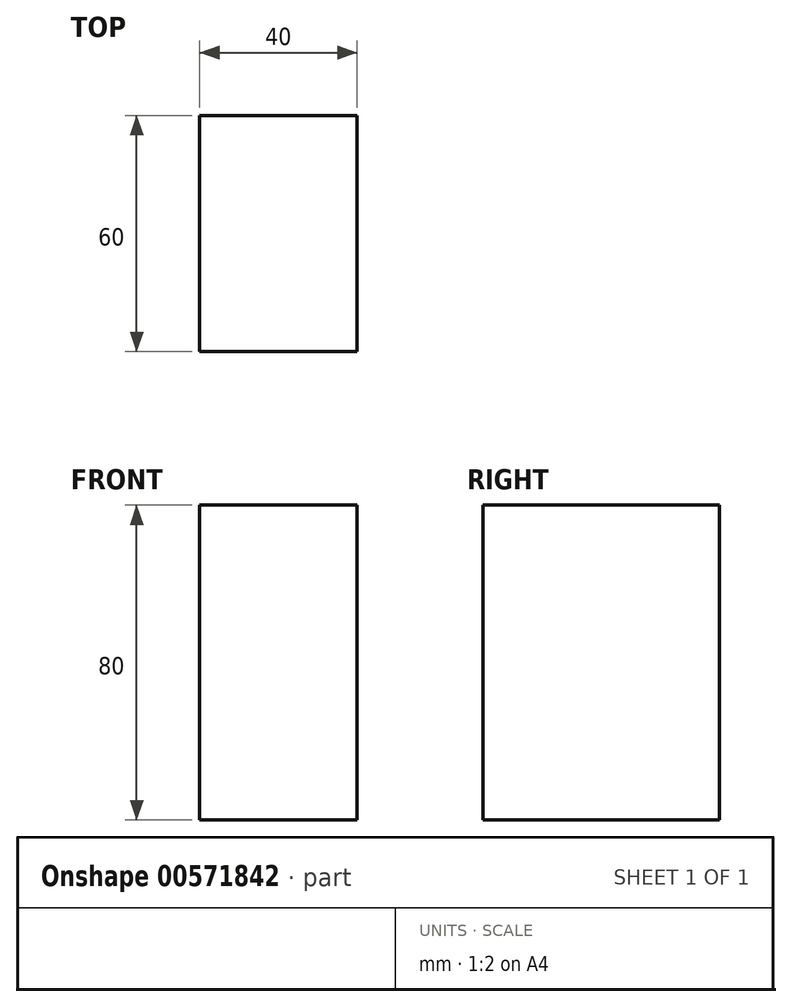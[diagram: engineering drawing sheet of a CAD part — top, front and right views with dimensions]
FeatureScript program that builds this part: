
annotation { "Feature Type Name" : "Feature", "Feature Type Description" : "" }
export const myFeature = defineFeature(function(context is Context, id is Id, definition is map)
    precondition{}
    {
        {
            var Q0;
            Q0=qCreatedBy(makeId("Top.planeOp"),FACE);
            var sketch = newSketch(context, id + "F0", { "sketchPlane" : qUnion([Q0])});
            skLineSegment(sketch, "E0.bottom", {"start": v(-46.22, 52.3) * mm, "end": v(-6.22, 52.3) * mm});
            skLineSegment(sketch, "E0.top", {"start": v(-46.22, -7.7) * mm, "end": v(-6.22, -7.7) * mm});
            skLineSegment(sketch, "E0.left", {"start": v(-46.22, 52.3) * mm, "end": v(-46.22, -7.7) * mm});
            skLineSegment(sketch, "E0.right", {"start": v(-6.22, 52.3) * mm, "end": v(-6.22, -7.7) * mm});
            skSolve(sketch);
        }
        {
            var Q0;
            Q0=makeQuery(id+"F0.imprint","IMPRINT",FACE,{"disambiguationData":[TD([[makeQuery(id+"F0.imprint","IMPRINT",EDGE,{"derivedFrom":sQuery(id+"F0.wireOp",EDGE,"E0.bottom")}),-1.0]])]});
            extrude(context, id + "F1", {"entities" : qUnion([Q0]), "depth" : 80 * mm, "offsetDistance" : 25 * mm});
        }
    });
